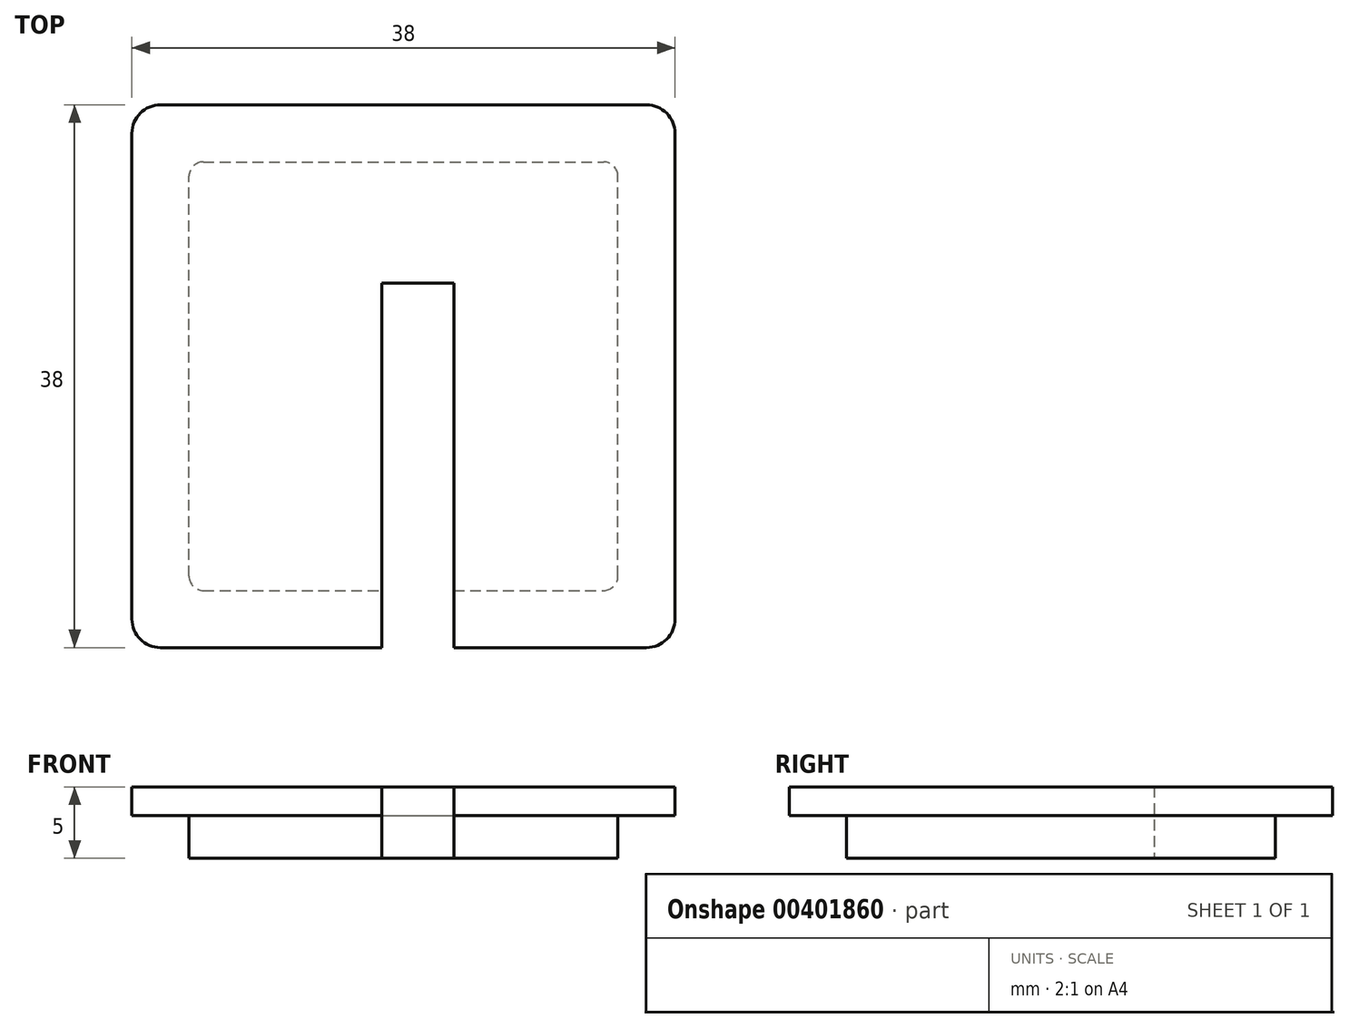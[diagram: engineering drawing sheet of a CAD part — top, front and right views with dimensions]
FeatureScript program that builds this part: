
annotation { "Feature Type Name" : "Feature", "Feature Type Description" : "" }
export const myFeature = defineFeature(function(context is Context, id is Id, definition is map)
    precondition{}
    {
        {
            var Q0;
            Q0=qCreatedBy(makeId("Top.planeOp"),FACE);
            var sketch = newSketch(context, id + "F0", { "sketchPlane" : qUnion([Q0])});
            skLineSegment(sketch, "E0.bottom", {"start": v(-17, 19) * mm, "end": v(17, 19) * mm});
            skLineSegment(sketch, "E0.top", {"start": v(-17, -19) * mm, "end": v(-1.5, -19) * mm});
            skLineSegment(sketch, "E0.left", {"start": v(-19, 17) * mm, "end": v(-19, -17) * mm});
            skLineSegment(sketch, "E0.right", {"start": v(19, 17) * mm, "end": v(19, -17) * mm});
            skLineSegment(sketch, "E1", {"start": v(-19, 0) * mm, "end": v(19, 0) * mm, "construction": true});
            skPoint(sketch, "E2", {"position": v(0, 0) * mm});
            skLineSegment(sketch, "E3.top", {"start": v(1.52, 6.52) * mm, "end": v(-1.5, 6.52) * mm});
            skLineSegment(sketch, "E3.right", {"start": v(-1.5, -19) * mm, "end": v(-1.5, 6.52) * mm});
            skLineSegment(sketch, "E4.MirrorCS", {"start": v(-1.52, 6.52) * mm, "end": v(1.5, 6.52) * mm});
            skPoint(sketch, "E5.MirrorCS.end.orphan", {"position": v(1.5, -19) * mm});
            skPoint(sketch, "E5.MirrorCS.start.orphan", {"position": v(0, -19) * mm});
            skLineSegment(sketch, "E6.trimOffspring", {"start": v(1.5, -19) * mm, "end": v(1.52, -19) * mm});
            skPoint(sketch, "E7.visualSharp", {"position": v(-19, 19) * mm});
            skArc(sketch, "E7.filletArc", {"start": v(-17, 19) * mm, "mid": v(-18.41, 18.41) * mm, "end": v(-19, 17) * mm});
            skPoint(sketch, "E8.visualSharp", {"position": v(19, 19) * mm});
            skArc(sketch, "E8.filletArc", {"start": v(19, 17) * mm, "mid": v(18.41, 18.41) * mm, "end": v(17, 19) * mm});
            skPoint(sketch, "E9.visualSharp", {"position": v(19, -19) * mm});
            skArc(sketch, "E9.filletArc", {"start": v(17, -19) * mm, "mid": v(18.41, -18.41) * mm, "end": v(19, -17) * mm});
            skPoint(sketch, "E10.visualSharp", {"position": v(-19, -19) * mm});
            skArc(sketch, "E10.filletArc", {"start": v(-19, -17) * mm, "mid": v(-18.41, -18.41) * mm, "end": v(-17, -19) * mm});
            skLineSegment(sketch, "E11.bottom", {"start": v(1.52, 6.52) * mm, "end": v(3.52, 6.52) * mm});
            skLineSegment(sketch, "E11.right", {"start": v(3.52, 6.52) * mm, "end": v(3.52, -19) * mm});
            skPoint(sketch, "E12.orphan", {"position": v(1.5, 6.52) * mm});
            skLineSegment(sketch, "E13.trimOffspring", {"start": v(3.52, -19) * mm, "end": v(17, -19) * mm});
            skSolve(sketch);
        }
        {
            var Q0;
            Q0 = qSketchRegion(id + "F0", true);
            extrude(context, id + "F1", {"entities" : qUnion([Q0]), "depth" : 2 * mm});
        }
        {
            var Q0;
            Q0=makeQuery(id+"F1.opExtrude","CAP_FACE",FACE,{"disambiguationData":[OSD([sQuery(id+"F0.wireOp",EDGE,"E0.bottom"),sQuery(id+"F0.wireOp",EDGE,"E0.top"),sQuery(id+"F0.wireOp",EDGE,"E0.left"),sQuery(id+"F0.wireOp",EDGE,"E0.right"),sQuery(id+"F0.wireOp",EDGE,"E3.top"),sQuery(id+"F0.wireOp",EDGE,"E3.right"),sQuery(id+"F0.wireOp",EDGE,"E4.MirrorCS"),sQuery(id+"F0.wireOp",EDGE,"6fca9d13-1a68-439b-8d81-e97f681ee5d30.MirrorCS"),sQuery(id+"F0.wireOp",EDGE,"E6.trimOffspring"),sQuery(id+"F0.wireOp",EDGE,"E7.filletArc"),sQuery(id+"F0.wireOp",EDGE,"E8.filletArc"),sQuery(id+"F0.wireOp",EDGE,"E9.filletArc"),sQuery(id+"F0.wireOp",EDGE,"E10.filletArc")])],"isStart":true});
            var sketch = newSketch(context, id + "F2", { "sketchPlane" : qUnion([Q0])});
            skLineSegment(sketch, "E14.bottom", {"start": v(-14, 15) * mm, "end": v(-1.5, 15) * mm});
            skLineSegment(sketch, "E14.top", {"start": v(-14, -15) * mm, "end": v(14, -15) * mm});
            skLineSegment(sketch, "E14.left", {"start": v(-15, 14) * mm, "end": v(-15, -14) * mm});
            skLineSegment(sketch, "E14.right", {"start": v(15, 14) * mm, "end": v(15, -14) * mm});
            skLineSegment(sketch, "E15", {"start": v(-19, 5.37) * mm, "end": v(-15, 5.37) * mm, "construction": true});
            skLineSegment(sketch, "E16", {"start": v(15, 5.37) * mm, "end": v(19, 5.37) * mm, "construction": true});
            skLineSegment(sketch, "E17", {"start": v(-6.66, 19) * mm, "end": v(-6.66, 15) * mm, "construction": true});
            skLineSegment(sketch, "E18", {"start": v(-6.66, -15) * mm, "end": v(-6.66, -19) * mm, "construction": true});
            skLineSegment(sketch, "E19", {"start": v(-1.5, 19) * mm, "end": v(-1.5, 15) * mm});
            skLineSegment(sketch, "E20", {"start": v(-1.5, 19) * mm, "end": v(-1.5, -6.52) * mm});
            skLineSegment(sketch, "E21", {"start": v(3.52, -6.52) * mm, "end": v(3.52, 15) * mm});
            skLineSegment(sketch, "E22.trimOffspring", {"start": v(3.52, 15) * mm, "end": v(14, 15) * mm});
            skLineSegment(sketch, "E23", {"start": v(-1.5, -6.52) * mm, "end": v(3.52, -6.52) * mm});
            skPoint(sketch, "E24.visualSharp", {"position": v(-15, 15) * mm});
            skArc(sketch, "E24.filletArc", {"start": v(-14, 15) * mm, "mid": v(-14.7, 14.7) * mm, "end": v(-15, 14) * mm});
            skPoint(sketch, "E25.visualSharp", {"position": v(15, 15) * mm});
            skArc(sketch, "E25.filletArc", {"start": v(15, 14) * mm, "mid": v(14.7, 14.7) * mm, "end": v(14, 15) * mm});
            skPoint(sketch, "E26.visualSharp", {"position": v(15, -15) * mm});
            skArc(sketch, "E26.filletArc", {"start": v(14, -15) * mm, "mid": v(14.7, -14.7) * mm, "end": v(15, -14) * mm});
            skPoint(sketch, "E27.visualSharp", {"position": v(-15, -15) * mm});
            skArc(sketch, "E27.filletArc", {"start": v(-15, -14) * mm, "mid": v(-14.7, -14.7) * mm, "end": v(-14, -15) * mm});
            skSolve(sketch);
        }
        {
            var Q0;
            Q0 = qSketchRegion(id + "F2", true);
            extrude(context, id + "F3", {"entities" : qUnion([Q0]), "operationType" : NewBodyOperationType.ADD, "depth" : 3 * mm});
        }
    });
